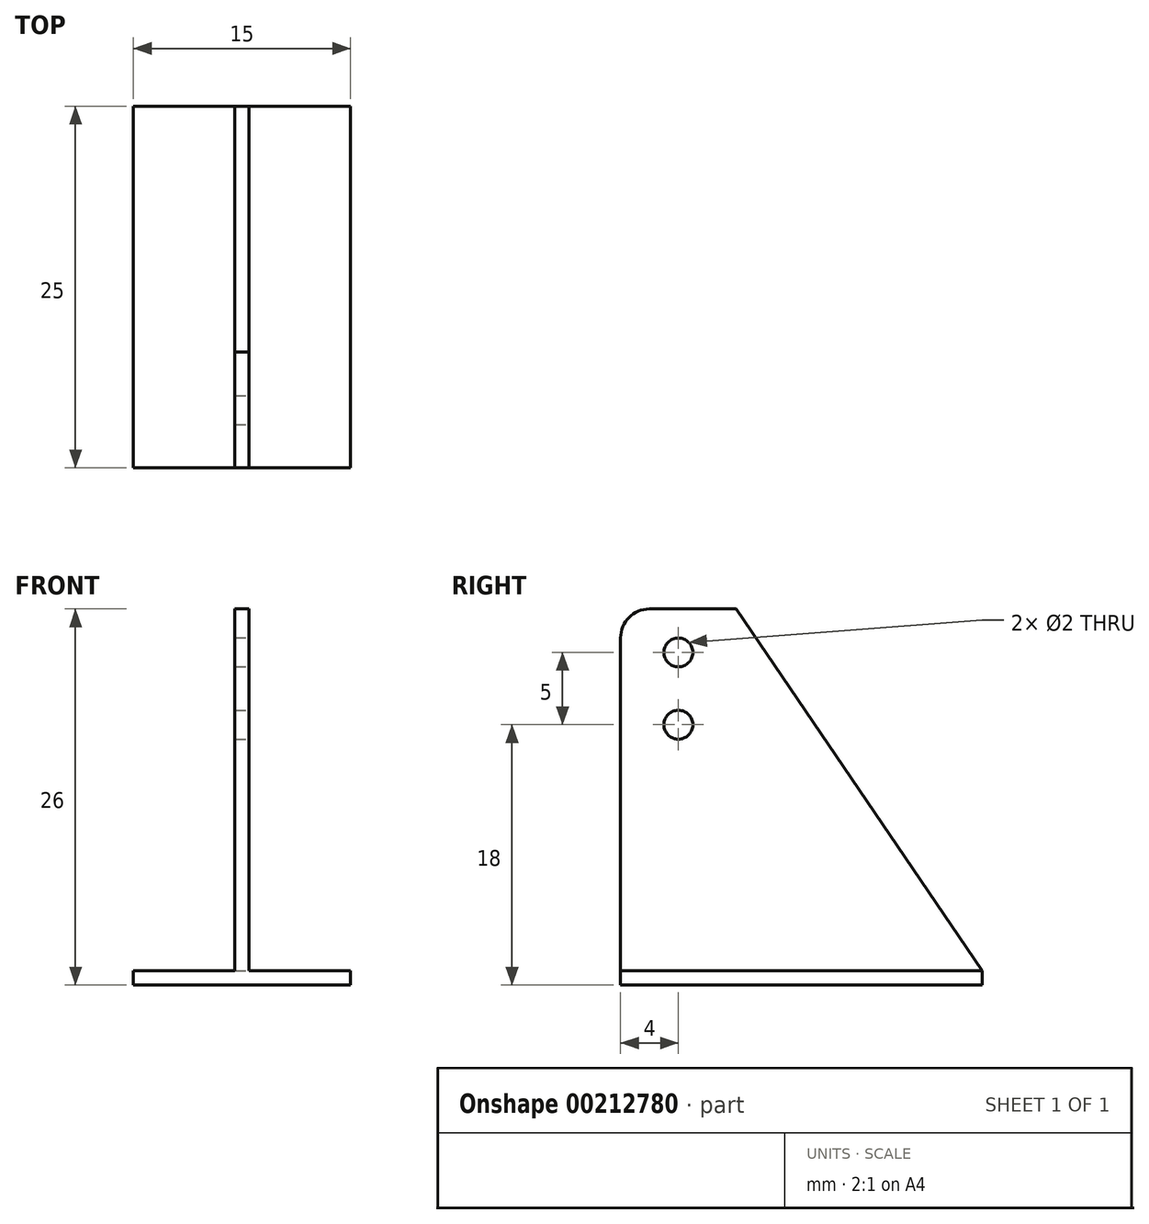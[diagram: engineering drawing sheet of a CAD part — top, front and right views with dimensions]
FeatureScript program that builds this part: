
annotation { "Feature Type Name" : "Feature", "Feature Type Description" : "" }
export const myFeature = defineFeature(function(context is Context, id is Id, definition is map)
    precondition{}
    {
        {
            var Q0;
            Q0=qCreatedBy(makeId("Top.planeOp"),FACE);
            var sketch = newSketch(context, id + "F0", { "sketchPlane" : qUnion([Q0])});
            skLineSegment(sketch, "E0.bottom", {"start": v(7.5, 12.5) * mm, "end": v(-7.5, 12.5) * mm});
            skLineSegment(sketch, "E0.top", {"start": v(7.5, -12.5) * mm, "end": v(-7.5, -12.5) * mm});
            skLineSegment(sketch, "E0.left", {"start": v(7.5, 12.5) * mm, "end": v(7.5, -12.5) * mm});
            skLineSegment(sketch, "E0.right", {"start": v(-7.5, 12.5) * mm, "end": v(-7.5, -12.5) * mm});
            skPoint(sketch, "E0.middle", {"position": v(0, 0) * mm});
            skSolve(sketch);
        }
        {
            var Q0;
            Q0 = qSketchRegion(id + "F0", true);
            extrude(context, id + "F1", {"entities" : qUnion([Q0]), "depth" : 1 * mm});
        }
        {
            var Q0;
            Q0=makeQuery(id+"F1.opExtrude","CAP_FACE",FACE,{"disambiguationData":[OSD([sQuery(id+"F0.wireOp",EDGE,"E0.bottom"),sQuery(id+"F0.wireOp",EDGE,"E0.top"),sQuery(id+"F0.wireOp",EDGE,"E0.left"),sQuery(id+"F0.wireOp",EDGE,"E0.right")])],"isStart":false});
            var sketch = newSketch(context, id + "F2", { "sketchPlane" : qUnion([Q0])});
            skLineSegment(sketch, "E1.bottom", {"start": v(0.5, 12.5) * mm, "end": v(-0.5, 12.5) * mm});
            skLineSegment(sketch, "E1.top", {"start": v(0.5, -12.5) * mm, "end": v(-0.5, -12.5) * mm});
            skLineSegment(sketch, "E1.left", {"start": v(0.5, 12.5) * mm, "end": v(0.5, -12.5) * mm});
            skLineSegment(sketch, "E1.right", {"start": v(-0.5, 12.5) * mm, "end": v(-0.5, -12.5) * mm});
            skPoint(sketch, "E1.middle", {"position": v(0, 0) * mm});
            skSolve(sketch);
        }
        {
            var Q0;
            Q0 = qSketchRegion(id + "F2", true);
            extrude(context, id + "F3", {"entities" : qUnion([Q0]), "operationType" : NewBodyOperationType.ADD, "depth" : 25 * mm});
        }
        {
            var Q0;
            Q0=makeQuery(id+"F3.opExtrude","SWEPT_FACE",FACE,{"disambiguationData":[OSD([sQuery(id+"F2.wireOp",EDGE,"E1.left")])]});
            var sketch = newSketch(context, id + "F4", { "sketchPlane" : qUnion([Q0])});
            skLineSegment(sketch, "E2", {"start": v(12.5, 1) * mm, "end": v(-4.5, 26) * mm});
            skLineSegment(sketch, "E3", {"start": v(-4.5, 26) * mm, "end": v(12.5, 26) * mm});
            skLineSegment(sketch, "E4", {"start": v(12.5, 26) * mm, "end": v(12.5, 1) * mm});
            skLineSegment(sketch, "E5", {"start": v(-8.5, 26) * mm, "end": v(-8.5, 1) * mm, "construction": true});
            skCircle(sketch, "E6", {"center": v(-8.5, 23) * mm, "radius": 1 * mm});
            skCircle(sketch, "E7", {"center": v(-8.5, 18) * mm, "radius": 1 * mm});
            skSolve(sketch);
        }
        {
            var Q0;
            Q0 = qSketchRegion(id + "F4", true);
            extrude(context, id + "F5", {"entities" : qUnion([Q0]), "operationType" : NewBodyOperationType.REMOVE, "endBound" : BoundingType.UP_TO_NEXT, "oppositeDirection" : true, "depth" : 25 * mm});
        }
        {
            var Q0;
            Q0=makeQuery(id+"F3.opExtrude","CAP_EDGE",EDGE,{"disambiguationData":[OSD([sQuery(id+"F2.wireOp",EDGE,"E1.top")])],"isStart":false});
            var Q1;
            Q1=makeQuery(id+"F5.boolean.opBoolean","COPY",EDGE,{"derivedFrom":makeQuery(id+"F5.opExtrude","SWEPT_EDGE",EDGE,{"disambiguationData":[OSD([sQuery(id+"F2.wireOp",EDGE,"E1.left"),sQuery(id+"F4.wireOp",EDGE,"E2"),sQuery(id+"F4.wireOp",EDGE,"E3")])]})});
            fillet(context, id + "F6", {"entities" : qUnion([Q0, Q1]), "radius" : 2 * mm, "tangentPropagation" : true, "allowEdgeOverflow" : false});
        }
    });
